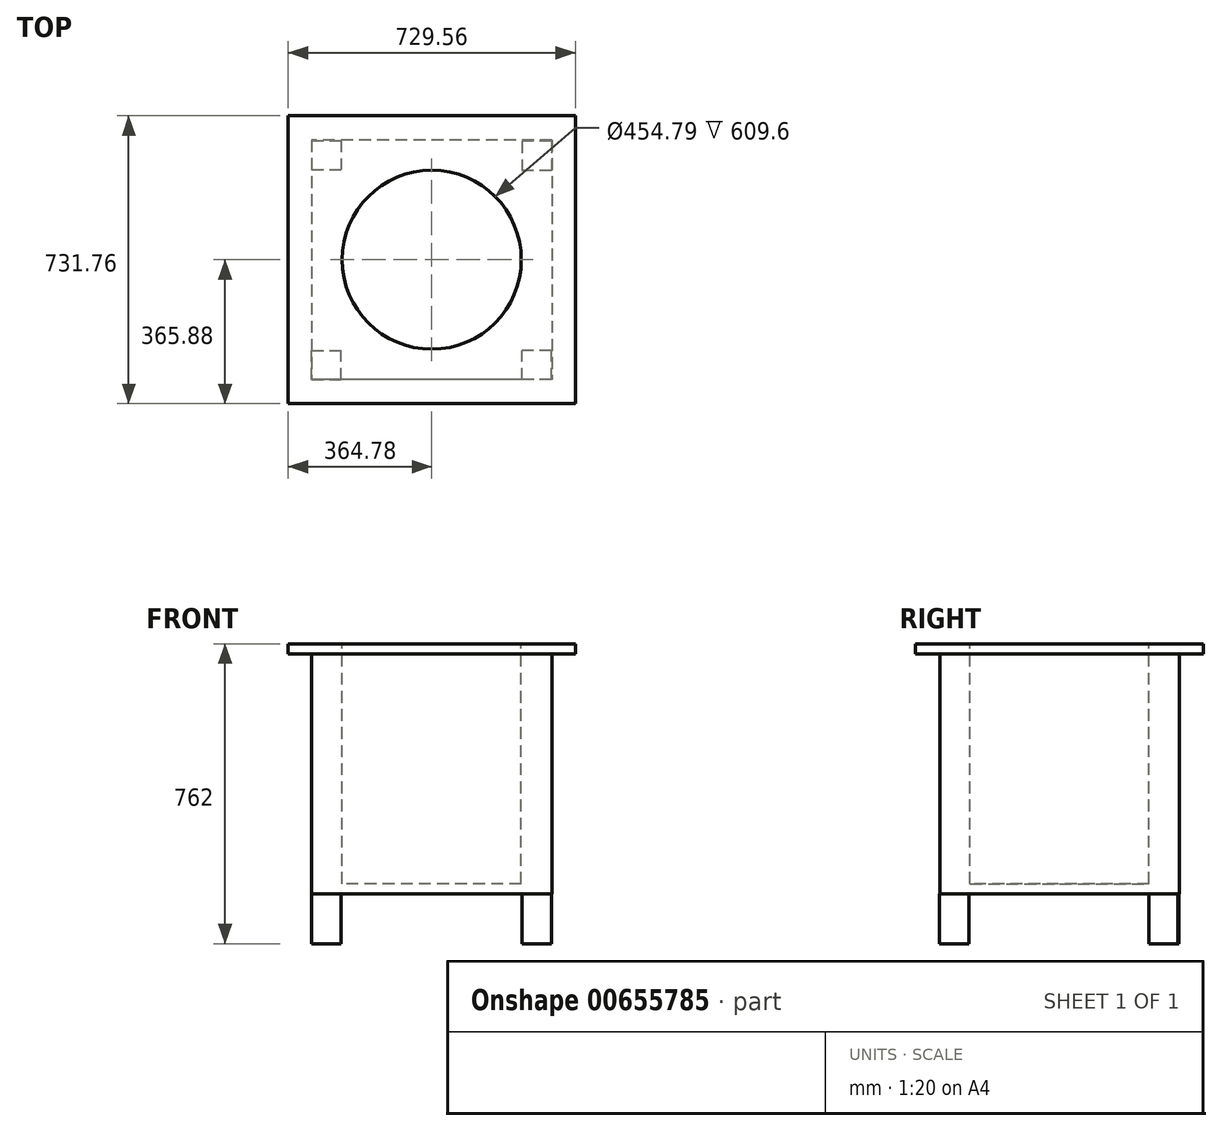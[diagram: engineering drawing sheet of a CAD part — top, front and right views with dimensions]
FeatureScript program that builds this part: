
annotation { "Feature Type Name" : "Feature", "Feature Type Description" : "" }
export const myFeature = defineFeature(function(context is Context, id is Id, definition is map)
    precondition{}
    {
        {
            var Q0;
            Q0=qCreatedBy(makeId("Top.planeOp"),FACE);
            var sketch = newSketch(context, id + "F0", { "sketchPlane" : qUnion([Q0])});
            skLineSegment(sketch, "E0.bottom", {"start": v(305.62, 304.47) * mm, "end": v(-305.62, 304.47) * mm});
            skLineSegment(sketch, "E0.top", {"start": v(305.62, -304.47) * mm, "end": v(-305.62, -304.47) * mm});
            skLineSegment(sketch, "E0.left", {"start": v(305.62, 304.47) * mm, "end": v(305.62, -304.47) * mm});
            skLineSegment(sketch, "E0.right", {"start": v(-305.62, 304.47) * mm, "end": v(-305.62, -304.47) * mm});
            skPoint(sketch, "E0.middle", {"position": v(0, 0) * mm});
            skSolve(sketch);
        }
        {
            var Q0;
            Q0 = qSketchRegion(id + "F0", true);
            extrude(context, id + "F1", {"entities" : qUnion([Q0]), "depth" : 609.6 * mm, "offsetDistance" : 25.4 * mm});
        }
        {
            var Q0;
            Q0=makeQuery(id+"F1.opExtrude","CAP_FACE",FACE,{"disambiguationData":[OSD([sQuery(id+"F0.wireOp",EDGE,"E0.bottom"),sQuery(id+"F0.wireOp",EDGE,"E0.top"),sQuery(id+"F0.wireOp",EDGE,"E0.left"),sQuery(id+"F0.wireOp",EDGE,"E0.right")])],"isStart":false});
            cPlane(context, id + "F2", {"entities" : qUnion([Q0]), "cplaneType" : CPlaneType.OFFSET, "offset" : 0 * mm, "width" : 152.4 * mm, "height" : 152.4 * mm});
        }
        {
            var Q0;
            Q0=qCreatedBy(id+"F2.planeOp",FACE);
            var sketch = newSketch(context, id + "F3", { "sketchPlane" : qUnion([Q0])});
            skLineSegment(sketch, "E1.bottom", {"start": v(364.78, 365.88) * mm, "end": v(-364.78, 365.88) * mm});
            skLineSegment(sketch, "E1.top", {"start": v(364.78, -365.88) * mm, "end": v(-364.78, -365.88) * mm});
            skLineSegment(sketch, "E1.left", {"start": v(364.78, 365.88) * mm, "end": v(364.78, -365.88) * mm});
            skLineSegment(sketch, "E1.right", {"start": v(-364.78, 365.88) * mm, "end": v(-364.78, -365.88) * mm});
            skPoint(sketch, "E1.middle", {"position": v(0, 0) * mm});
            skSolve(sketch);
        }
        {
            var Q0;
            Q0 = qSketchRegion(id + "F3", true);
            extrude(context, id + "F4", {"entities" : qUnion([Q0]), "operationType" : NewBodyOperationType.ADD, "depth" : 25.4 * mm, "offsetDistance" : 25.4 * mm});
        }
        {
            var Q0;
            Q0=makeQuery(id+"F4.opExtrude","CAP_FACE",FACE,{"disambiguationData":[OSD([sQuery(id+"F3.wireOp",EDGE,"E1.bottom"),sQuery(id+"F3.wireOp",EDGE,"E1.top"),sQuery(id+"F3.wireOp",EDGE,"E1.left"),sQuery(id+"F3.wireOp",EDGE,"E1.right")])],"isStart":false});
            cPlane(context, id + "F5", {"entities" : qUnion([Q0]), "cplaneType" : CPlaneType.OFFSET, "offset" : 0 * mm, "width" : 152.4 * mm, "height" : 152.4 * mm});
        }
        {
            var Q0;
            Q0=qCreatedBy(id+"F5.planeOp",FACE);
            var sketch = newSketch(context, id + "F6", { "sketchPlane" : qUnion([Q0])});
            skCircle(sketch, "E2", {"center": v(0, 0) * mm, "radius": 227.4 * mm});
            skSolve(sketch);
        }
        {
            var Q0;
            Q0=makeQuery(id+"F6.imprint","IMPRINT",FACE,{"disambiguationData":[TD([[makeQuery(id+"F6.imprint","IMPRINT",EDGE,{"derivedFrom":sQuery(id+"F6.wireOp",EDGE,"E2")}),1.0]])]});
            extrude(context, id + "F7", {"entities" : qUnion([Q0]), "operationType" : NewBodyOperationType.REMOVE, "oppositeDirection" : true, "depth" : 609.6 * mm, "offsetDistance" : 25.4 * mm});
        }
        {
            var Q0;
            Q0=makeQuery(id+"F1.opExtrude","CAP_FACE",FACE,{"disambiguationData":[OSD([sQuery(id+"F0.wireOp",EDGE,"E0.bottom"),sQuery(id+"F0.wireOp",EDGE,"E0.top"),sQuery(id+"F0.wireOp",EDGE,"E0.left"),sQuery(id+"F0.wireOp",EDGE,"E0.right")])],"isStart":true});
            cPlane(context, id + "F8", {"entities" : qUnion([Q0]), "cplaneType" : CPlaneType.OFFSET, "offset" : 0 * mm, "width" : 152.4 * mm, "height" : 152.4 * mm});
        }
        {
            var Q0;
            Q0=qCreatedBy(id+"F8.planeOp",FACE);
            var sketch = newSketch(context, id + "F9", { "sketchPlane" : qUnion([Q0])});
            skLineSegment(sketch, "E3.bottom", {"start": v(-305.16, 304.79) * mm, "end": v(-230.86, 304.79) * mm});
            skLineSegment(sketch, "E3.top", {"start": v(-305.16, 230.48) * mm, "end": v(-230.86, 230.48) * mm});
            skLineSegment(sketch, "E3.left", {"start": v(-305.16, 304.79) * mm, "end": v(-305.16, 230.48) * mm});
            skLineSegment(sketch, "E3.right", {"start": v(-230.86, 304.79) * mm, "end": v(-230.86, 230.48) * mm});
            skLineSegment(sketch, "E4.bottom", {"start": v(303.9, 304.79) * mm, "end": v(229.6, 304.79) * mm});
            skLineSegment(sketch, "E4.top", {"start": v(303.9, 230.48) * mm, "end": v(229.6, 230.48) * mm});
            skLineSegment(sketch, "E4.left", {"start": v(303.9, 304.79) * mm, "end": v(303.9, 230.48) * mm});
            skLineSegment(sketch, "E4.right", {"start": v(229.6, 304.79) * mm, "end": v(229.6, 230.48) * mm});
            skLineSegment(sketch, "E5.bottom", {"start": v(303.9, -300.9) * mm, "end": v(229.6, -300.9) * mm});
            skLineSegment(sketch, "E5.top", {"start": v(303.9, -226.59) * mm, "end": v(229.6, -226.59) * mm});
            skLineSegment(sketch, "E5.left", {"start": v(303.9, -300.9) * mm, "end": v(303.9, -226.59) * mm});
            skLineSegment(sketch, "E5.right", {"start": v(229.6, -300.9) * mm, "end": v(229.6, -226.59) * mm});
            skLineSegment(sketch, "E6.bottom", {"start": v(-305.16, -303.14) * mm, "end": v(-230.86, -303.14) * mm});
            skLineSegment(sketch, "E6.top", {"start": v(-305.16, -228.84) * mm, "end": v(-230.86, -228.84) * mm});
            skLineSegment(sketch, "E6.left", {"start": v(-305.16, -303.14) * mm, "end": v(-305.16, -228.84) * mm});
            skLineSegment(sketch, "E6.right", {"start": v(-230.86, -303.14) * mm, "end": v(-230.86, -228.84) * mm});
            skSolve(sketch);
        }
        {
            var Q0;
            Q0 = qSketchRegion(id + "F9", true);
            extrude(context, id + "F10", {"entities" : qUnion([Q0]), "operationType" : NewBodyOperationType.ADD, "depth" : 127 * mm, "offsetDistance" : 25.4 * mm});
        }
    });
